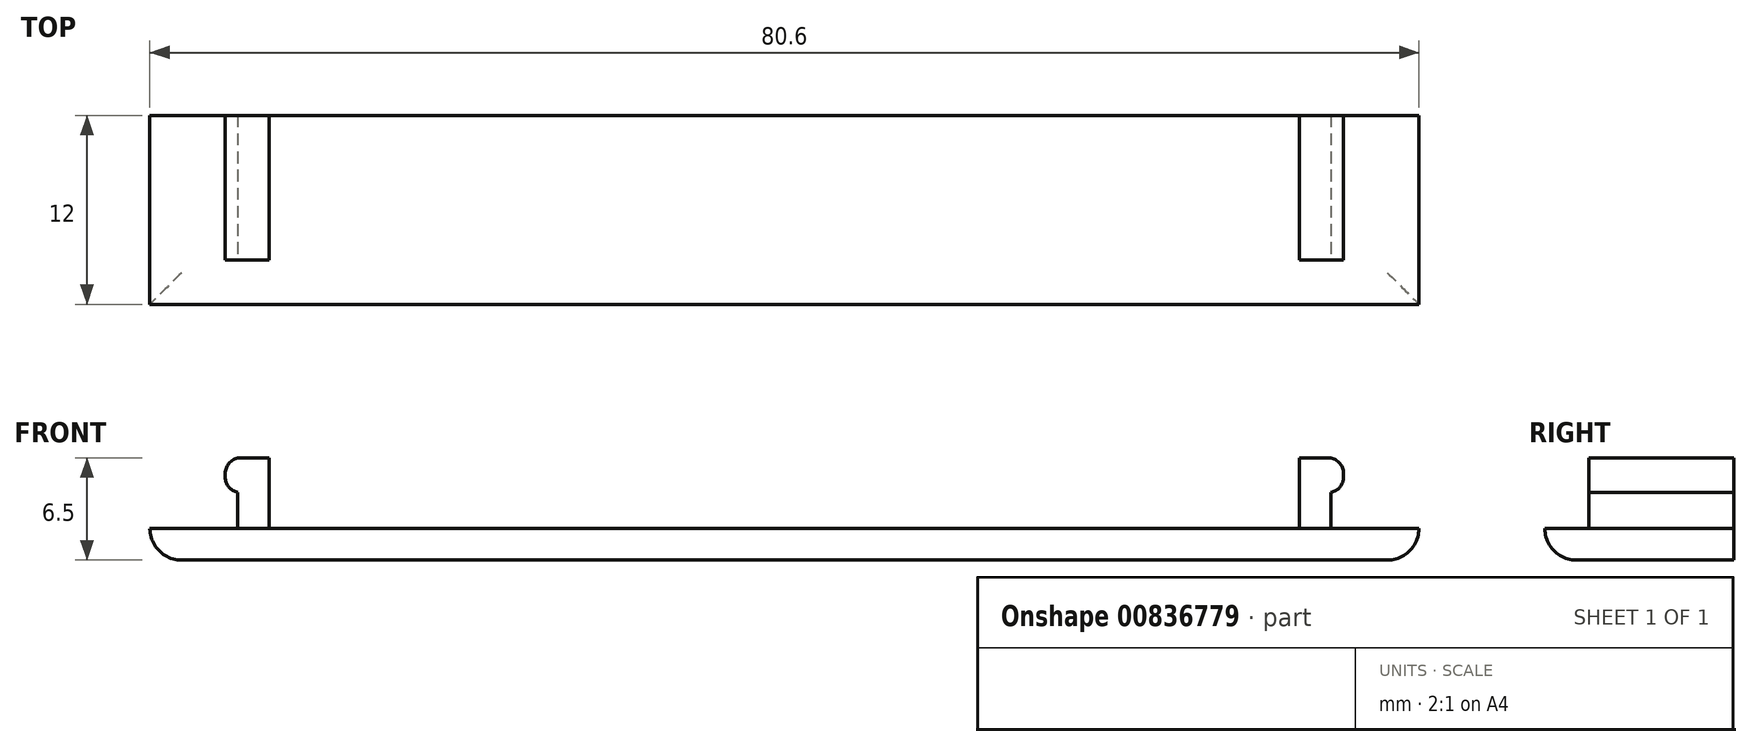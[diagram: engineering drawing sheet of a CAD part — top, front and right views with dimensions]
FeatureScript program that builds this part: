
annotation { "Feature Type Name" : "Feature", "Feature Type Description" : "" }
export const myFeature = defineFeature(function(context is Context, id is Id, definition is map)
    precondition{}
    {
        {
            var Q0;
            Q0=qCreatedBy(makeId("Top.planeOp"),FACE);
            var sketch = newSketch(context, id + "F0", { "sketchPlane" : qUnion([Q0])});
            skLineSegment(sketch, "E0.bottom", {"start": v(0, 0) * mm, "end": v(-80.6, 0) * mm});
            skLineSegment(sketch, "E0.top", {"start": v(0, 12) * mm, "end": v(-80.6, 12) * mm});
            skLineSegment(sketch, "E0.left", {"start": v(0, 0) * mm, "end": v(0, 12) * mm});
            skLineSegment(sketch, "E0.right", {"start": v(-80.6, 0) * mm, "end": v(-80.6, 12) * mm});
            skSolve(sketch);
        }
        {
            var Q0;
            Q0=makeQuery(id+"F0.imprint","IMPRINT",FACE,{"disambiguationData":[TD([[makeQuery(id+"F0.imprint","IMPRINT",EDGE,{"derivedFrom":sQuery(id+"F0.wireOp",EDGE,"E0.bottom")}),-1.0]])]});
            extrude(context, id + "F1", {"entities" : qUnion([Q0]), "oppositeDirection" : true, "depth" : 2 * mm, "offsetDistance" : 25 * mm});
        }
        {
            var Q0;
            Q0=makeQuery(id+"F1.opExtrude","CAP_FACE",FACE,{"disambiguationData":[OSD([sQuery(id+"F0.wireOp",EDGE,"E0.bottom"),sQuery(id+"F0.wireOp",EDGE,"E0.top"),sQuery(id+"F0.wireOp",EDGE,"E0.left"),sQuery(id+"F0.wireOp",EDGE,"E0.right")])],"isStart":true});
            var sketch = newSketch(context, id + "F2", { "sketchPlane" : qUnion([Q0])});
            skLineSegment(sketch, "E1.bottom", {"start": v(-75.02, 12) * mm, "end": v(-73.02, 12) * mm});
            skLineSegment(sketch, "E1.top", {"start": v(-75.02, 2.8) * mm, "end": v(-73.02, 2.8) * mm});
            skLineSegment(sketch, "E1.left", {"start": v(-75.02, 12) * mm, "end": v(-75.02, 2.8) * mm});
            skLineSegment(sketch, "E1.right", {"start": v(-73.02, 12) * mm, "end": v(-73.02, 2.8) * mm});
            skLineSegment(sketch, "E2.bottom", {"start": v(-5.58, 12) * mm, "end": v(-7.58, 12) * mm});
            skLineSegment(sketch, "E2.top", {"start": v(-5.58, 2.8) * mm, "end": v(-7.58, 2.8) * mm});
            skLineSegment(sketch, "E2.left", {"start": v(-5.58, 12) * mm, "end": v(-5.58, 2.8) * mm});
            skLineSegment(sketch, "E2.right", {"start": v(-7.58, 12) * mm, "end": v(-7.58, 2.8) * mm});
            skSolve(sketch);
        }
        {
            var Q0;
            Q0=makeQuery(id+"F2.imprint","IMPRINT",FACE,{"disambiguationData":[TD([[makeQuery(id+"F2.imprint","IMPRINT",EDGE,{"derivedFrom":sQuery(id+"F2.wireOp",EDGE,"E1.bottom")}),1.0]])]});
            var Q1;
            Q1=makeQuery(id+"F2.imprint","IMPRINT",FACE,{"disambiguationData":[TD([[makeQuery(id+"F2.imprint","IMPRINT",EDGE,{"derivedFrom":sQuery(id+"F2.wireOp",EDGE,"E2.bottom")}),1.0]])]});
            extrude(context, id + "F3", {"entities" : qUnion([Q0, Q1]), "operationType" : NewBodyOperationType.ADD, "depth" : 4.5 * mm, "offsetDistance" : 25 * mm});
        }
        {
            var Q0;
            Q0=makeQuery(id+"F3.opExtrude","SWEPT_FACE",FACE,{"disambiguationData":[OSD([sQuery(id+"F2.wireOp",EDGE,"E1.left")])]});
            var sketch = newSketch(context, id + "F4", { "sketchPlane" : qUnion([Q0])});
            skLineSegment(sketch, "E3.bottom", {"start": v(-12, 4.5) * mm, "end": v(-2.8, 4.5) * mm});
            skLineSegment(sketch, "E3.top", {"start": v(-12, 2.3) * mm, "end": v(-2.8, 2.3) * mm});
            skLineSegment(sketch, "E3.left", {"start": v(-12, 4.5) * mm, "end": v(-12, 2.3) * mm});
            skLineSegment(sketch, "E3.right", {"start": v(-2.8, 4.5) * mm, "end": v(-2.8, 2.3) * mm});
            skSolve(sketch);
        }
        {
            var Q0;
            Q0=makeQuery(id+"F4.imprint","IMPRINT",FACE,{"disambiguationData":[TD([[makeQuery(id+"F4.imprint","IMPRINT",EDGE,{"derivedFrom":sQuery(id+"F4.wireOp",EDGE,"E3.bottom")}),-1.0]])]});
            extrude(context, id + "F5", {"entities" : qUnion([Q0]), "operationType" : NewBodyOperationType.ADD, "depth" : .8 * mm, "offsetDistance" : 25 * mm});
        }
        {
            var Q0;
            Q0=makeQuery(id+"F1.opExtrude","CAP_EDGE",EDGE,{"disambiguationData":[OSD([sQuery(id+"F0.wireOp",EDGE,"E0.right")])],"isStart":false});
            var Q1;
            Q1=makeQuery(id+"F1.opExtrude","CAP_EDGE",EDGE,{"disambiguationData":[OSD([sQuery(id+"F0.wireOp",EDGE,"E0.left")])],"isStart":false});
            var Q2;
            Q2=makeQuery(id+"F1.opExtrude","CAP_EDGE",EDGE,{"disambiguationData":[OSD([sQuery(id+"F0.wireOp",EDGE,"E0.bottom")])],"isStart":false});
            fillet(context, id + "F6", {"entities" : qUnion([Q0, Q1, Q2]), "radius" : 2 * mm, "tangentPropagation" : true, "allowEdgeOverflow" : false});
        }
        {
            var Q0;
            Q0=makeQuery(id+"F3.opExtrude","SWEPT_FACE",FACE,{"disambiguationData":[OSD([sQuery(id+"F2.wireOp",EDGE,"E2.left")])]});
            var sketch = newSketch(context, id + "F7", { "sketchPlane" : qUnion([Q0])});
            skLineSegment(sketch, "E4.bottom", {"start": v(12, 4.5) * mm, "end": v(2.8, 4.5) * mm});
            skLineSegment(sketch, "E4.top", {"start": v(12, 2.3) * mm, "end": v(2.8, 2.3) * mm});
            skLineSegment(sketch, "E4.left", {"start": v(12, 4.5) * mm, "end": v(12, 2.3) * mm});
            skLineSegment(sketch, "E4.right", {"start": v(2.8, 4.5) * mm, "end": v(2.8, 2.3) * mm});
            skSolve(sketch);
        }
        {
            var Q0;
            Q0=makeQuery(id+"F7.imprint","IMPRINT",FACE,{"disambiguationData":[TD([[makeQuery(id+"F7.imprint","IMPRINT",EDGE,{"derivedFrom":sQuery(id+"F7.wireOp",EDGE,"E4.bottom")}),1.0]])]});
            extrude(context, id + "F8", {"entities" : qUnion([Q0]), "operationType" : NewBodyOperationType.ADD, "depth" : .8 * mm, "offsetDistance" : 25 * mm});
        }
        {
            var Q0;
            Q0=makeQuery(id+"F8.opExtrude","CAP_EDGE",EDGE,{"disambiguationData":[OSD([sQuery(id+"F7.wireOp",EDGE,"E4.top")])],"isStart":false});
            var Q1;
            Q1=makeQuery(id+"F8.opExtrude","CAP_EDGE",EDGE,{"disambiguationData":[OSD([sQuery(id+"F7.wireOp",EDGE,"E4.bottom")])],"isStart":false});
            var Q2;
            Q2=makeQuery(id+"F5.opExtrude","CAP_EDGE",EDGE,{"disambiguationData":[OSD([sQuery(id+"F4.wireOp",EDGE,"E3.top")])],"isStart":false});
            var Q3;
            Q3=makeQuery(id+"F5.opExtrude","CAP_EDGE",EDGE,{"disambiguationData":[OSD([sQuery(id+"F4.wireOp",EDGE,"E3.bottom")])],"isStart":false});
            fillet(context, id + "F9", {"entities" : qUnion([Q0, Q1, Q2, Q3]), "radius" : 1 * mm, "tangentPropagation" : true, "allowEdgeOverflow" : false});
        }
    });
